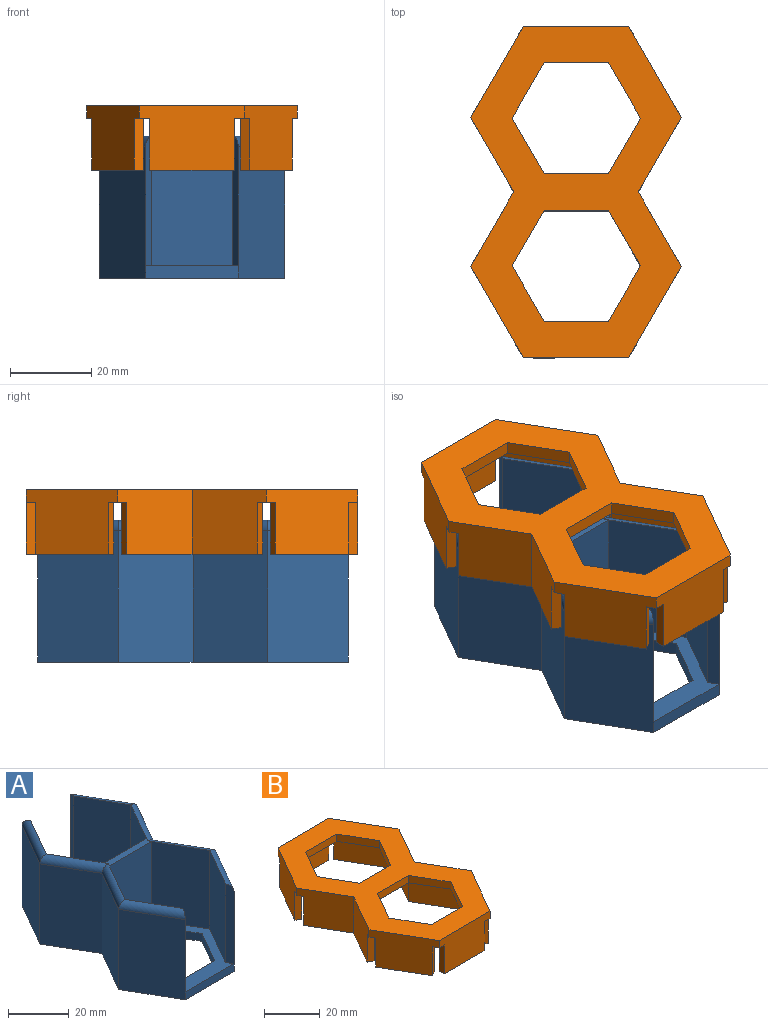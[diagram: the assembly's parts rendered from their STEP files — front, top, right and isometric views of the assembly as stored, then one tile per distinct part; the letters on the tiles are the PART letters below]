
ASSEMBLY  parts=2 mates=2
PART A: 48 faces, bbox 45.5x76.2x34.9 mm
  f0: plane 19.8x2.54mm, normal (0,0,1), area 48.4mm2, adj f4,f6,f41,f42,f45,f46
  f1: plane 31.75x17.15mm, normal (0.87,-0.5,0), area 628.6mm2, adj f20,f28,f37,f40
  f2: plane 31.75x17.15mm, normal (-0.87,-0.5,0), area 628.6mm2, adj f3,f28,f36,f47
  f3: plane 31.75x17.15mm, normal (-0.87,0.5,0), area 628.6mm2, adj f2,f4,f28,f46
  f4: plane 31.75x19.8mm, normal (0,1,0), area 628.6mm2, adj f0,f3,f20,f28
  f5: plane 31.75x17.15mm, normal (0.87,-0.5,0), area 628.6mm2, adj f6,f18,f35,f42
  f6: plane 31.75x19.8mm, normal (0,-1,0), area 628.6mm2, adj f0,f5,f7,f35
  f7: plane 31.75x17.15mm, normal (-0.87,-0.5,0), area 628.6mm2, adj f6,f8,f35,f45
  f8: plane 31.75x17.15mm, normal (-0.87,0.5,0), area 628.6mm2, adj f7,f35,f39,f44
  f9: plane 32.39x19.69mm, normal (0.87,-0.5,0), area 736.1mm2, adj f10,f19,f21,f39,f44
  f10: plane 32.39x18.42mm, normal (0.87,0.5,0), area 688.6mm2, adj f9,f11,f21,f45
  f11: plane 32.39x18.42mm, normal (0.87,-0.5,0), area 688.6mm2, adj f10,f12,f21,f46
  f12: plane 32.39x19.69mm, normal (0.87,0.5,0), area 736.1mm2, adj f11,f13,f21,f36,f47
  f13: plane 22.73x3.18mm, normal (0,1,0), area 72.2mm2, adj f12,f14,f21,f28
  f14: plane 32.39x19.69mm, normal (-0.87,0.5,0), area 736.1mm2, adj f13,f15,f21,f37,f40
  f15: plane 32.39x18.42mm, normal (-0.87,-0.5,0), area 688.6mm2, adj f14,f16,f21,f41
  f16: plane 32.39x18.42mm, normal (-0.87,0.5,0), area 688.6mm2, adj f15,f17,f21,f42
  f17: plane 32.39x19.69mm, normal (-0.87,-0.5,0), area 736.1mm2, adj f16,f19,f21,f38,f43
  f18: plane 31.75x17.15mm, normal (0.87,0.5,0), area 628.6mm2, adj f5,f35,f38,f43
  f19: plane 22.73x3.18mm, normal (0,-1,0), area 72.2mm2, adj f9,f17,f21,f35
  f20: plane 31.75x17.15mm, normal (0.87,0.5,0), area 628.6mm2, adj f1,f4,f28,f41
  f21: plane 76.2x45.46mm, normal (0,0,-1), area 1273mm2, adj f9,f10,f11,f12,f13,f14,f15,f16
  f22: plane 13.97x8.07mm, normal (-0.87,0.5,0), area 51.2mm2, adj f21,f23,f27,f28
  f23: plane 16.13x3.18mm, normal (0,1,0), area 51.2mm2, adj f21,f22,f24,f28
  f24: plane 13.97x8.07mm, normal (0.87,0.5,0), area 51.2mm2, adj f21,f23,f25,f28
  f25: plane 13.97x8.07mm, normal (0.87,-0.5,0), area 51.2mm2, adj f21,f24,f26,f28
  f26: plane 16.13x3.18mm, normal (0,-1,0), area 51.2mm2, adj f21,f25,f27,f28
  f27: plane 13.97x8.07mm, normal (-0.87,-0.5,0), area 51.2mm2, adj f21,f22,f26,f28
  f28: plane 39.59x36.83mm, normal (0,0,1), area 396.2mm2, adj f1,f2,f3,f4,f13,f20,f22,f23
  f29: plane 13.97x8.07mm, normal (-0.87,0.5,0), area 51.2mm2, adj f21,f30,f34,f35
  f30: plane 16.13x3.18mm, normal (0,1,0), area 51.2mm2, adj f21,f29,f31,f35
  f31: plane 13.97x8.07mm, normal (0.87,0.5,0), area 51.2mm2, adj f21,f30,f32,f35
  f32: plane 13.97x8.07mm, normal (0.87,-0.5,0), area 51.2mm2, adj f21,f31,f33,f35
  f33: plane 16.13x3.18mm, normal (0,-1,0), area 51.2mm2, adj f21,f32,f34,f35
  f34: plane 13.97x8.07mm, normal (-0.87,-0.5,0), area 51.2mm2, adj f21,f29,f33,f35
  f35: plane 39.59x36.83mm, normal (0,0,1), area 396.2mm2, adj f5,f6,f7,f8,f18,f19,f29,f30
  f36: plane 31.75x2.54mm, normal (-0.87,0.5,0), area 91.5mm2, adj f2,f12,f28,f47
  f37: plane 31.75x2.54mm, normal (0.87,0.5,0), area 91.5mm2, adj f1,f14,f28,f40
  f38: plane 31.75x2.54mm, normal (0.87,-0.5,0), area 91.5mm2, adj f17,f18,f35,f43
  f39: plane 31.75x2.54mm, normal (-0.87,-0.5,0), area 91.5mm2, adj f8,f9,f35,f44
  f40: cylinder r=2.54mm len=20.96mm, axis (0.5,0.87,0), area 86.4mm2, adj f1,f14,f37,f41
  f41: cylinder r=2.54mm len=20.96mm, axis (-0.5,0.87,0), area 84.8mm2, adj f0,f15,f20,f40,f42
  f42: cylinder r=2.54mm len=20.96mm, axis (0.5,0.87,0), area 84.8mm2, adj f0,f5,f16,f41,f43
  f43: cylinder r=2.54mm len=20.96mm, axis (-0.5,0.87,0), area 86.4mm2, adj f17,f18,f38,f42
  f44: cylinder r=2.54mm len=20.96mm, axis (-0.5,-0.87,0), area 86.4mm2, adj f8,f9,f39,f45
  f45: cylinder r=2.54mm len=20.96mm, axis (0.5,-0.87,0), area 84.8mm2, adj f0,f7,f10,f44,f46
  f46: cylinder r=2.54mm len=20.96mm, axis (-0.5,-0.87,0), area 84.8mm2, adj f0,f3,f11,f45,f47
  f47: cylinder r=2.54mm len=20.96mm, axis (0.5,-0.87,0), area 86.4mm2, adj f2,f12,f36,f46
PART B: 58 faces, bbox 51.8x81.5x15.9 mm
  f0: plane 19.35x12.64mm, normal (0,0,-1), area 53mm2, adj f18,f21,f42,f44
  f1: plane 19.35x12.64mm, normal (0,0,-1), area 53mm2, adj f13,f16,f46,f49
  f2: plane 34.72x12.22mm, normal (0,0,-1), area 98.1mm2, adj f14,f20,f26,f29,f47,f55
  f3: plane 20.73x2.54mm, normal (0,0,-1), area 52.7mm2, adj f9,f24,f52,f56
  f4: plane 19.35x12.64mm, normal (0,0,-1), area 53mm2, adj f8,f25,f54,f57
  f5: plane 19.35x12.64mm, normal (0,0,-1), area 53mm2, adj f10,f11,f50,f53
  f6: plane 34.72x12.22mm, normal (0,0,-1), area 98.1mm2, adj f15,f19,f27,f28,f43,f51
  f7: plane 20.73x2.54mm, normal (0,0,-1), area 52.7mm2, adj f12,f17,f45,f48
  f8: plane 18.08x12.7mm, normal (0.87,-0.5,0), area 265.1mm2, adj f4,f22,f54,f57
  f9: plane 20.73x12.7mm, normal (0,-1,0), area 263.3mm2, adj f3,f22,f52,f56
  f10: plane 18.08x12.7mm, normal (-0.87,-0.5,0), area 265.1mm2, adj f5,f22,f50,f53
  f11: plane 22.48x15.88mm, normal (0.87,0.5,0), area 347.5mm2, adj f5,f22,f23,f24,f27,f50,f53
  f12: plane 25.81x15.88mm, normal (0,-1,0), area 345.2mm2, adj f7,f13,f21,f22,f23,f45,f48
  f13: plane 22.48x15.88mm, normal (-0.87,-0.5,0), area 347.5mm2, adj f1,f12,f14,f22,f23,f46,f49
  f14: plane 18.29x15.88mm, normal (-0.87,0.5,0), area 303mm2, adj f2,f13,f22,f23,f26,f47
  f15: plane 18.29x15.88mm, normal (0.87,0.5,0), area 303mm2, adj f6,f21,f22,f23,f27,f43
  f16: plane 18.08x12.7mm, normal (0.87,0.5,0), area 265.1mm2, adj f1,f22,f46,f49
  f17: plane 20.73x12.7mm, normal (0,1,0), area 263.3mm2, adj f7,f22,f45,f48
  f18: plane 18.08x12.7mm, normal (-0.87,0.5,0), area 265.1mm2, adj f0,f22,f42,f44
  f19: plane 17.36x12.7mm, normal (-0.87,-0.5,0), area 254.6mm2, adj f6,f22,f28,f43
  f20: plane 17.36x12.7mm, normal (0.87,-0.5,0), area 254.6mm2, adj f2,f22,f29,f47
  f21: plane 22.48x15.88mm, normal (0.87,-0.5,0), area 347.5mm2, adj f0,f12,f15,f22,f23,f42,f44
  f22: plane 81.53x51.77mm, normal (0,0,-1), area 1444.3mm2, adj f8,f9,f10,f11,f12,f13,f14,f15
  f23: plane 81.53x51.77mm, normal (0,0,1), area 1957.9mm2, adj f11,f12,f13,f14,f15,f21,f24,f25
  f24: plane 25.81x15.88mm, normal (0,1,0), area 345.2mm2, adj f3,f11,f22,f23,f25,f52,f56
  f25: plane 22.48x15.88mm, normal (-0.87,0.5,0), area 347.5mm2, adj f4,f22,f23,f24,f26,f54,f57
  f26: plane 18.29x15.88mm, normal (-0.87,-0.5,0), area 303mm2, adj f2,f14,f22,f23,f25,f55
  f27: plane 18.29x15.88mm, normal (0.87,-0.5,0), area 303mm2, adj f6,f11,f15,f22,f23,f51
  f28: plane 17.36x12.7mm, normal (-0.87,0.5,0), area 254.6mm2, adj f6,f19,f22,f51
  f29: plane 17.36x12.7mm, normal (0.87,0.5,0), area 254.6mm2, adj f2,f20,f22,f55
  f30: plane 13.66x7.89mm, normal (-0.87,-0.5,0), area 50.1mm2, adj f22,f23,f31,f35
  f31: plane 15.78x3.18mm, normal (0,-1,0), area 50.1mm2, adj f22,f23,f30,f32
  f32: plane 13.66x7.89mm, normal (0.87,-0.5,0), area 50.1mm2, adj f22,f23,f31,f33
  f33: plane 13.66x7.89mm, normal (0.87,0.5,0), area 50.1mm2, adj f22,f23,f32,f34
  f34: plane 15.78x3.18mm, normal (0,1,0), area 50.1mm2, adj f22,f23,f33,f35
  f35: plane 13.66x7.89mm, normal (-0.87,0.5,0), area 50.1mm2, adj f22,f23,f30,f34
  f36: plane 13.66x7.89mm, normal (-0.87,0.5,0), area 50.1mm2, adj f22,f23,f37,f41
  f37: plane 15.78x3.18mm, normal (0,1,0), area 50.1mm2, adj f22,f23,f36,f38
  f38: plane 13.66x7.89mm, normal (0.87,0.5,0), area 50.1mm2, adj f22,f23,f37,f39
  f39: plane 13.66x7.89mm, normal (0.87,-0.5,0), area 50.1mm2, adj f22,f23,f38,f40
  f40: plane 15.78x3.18mm, normal (0,-1,0), area 50.1mm2, adj f22,f23,f39,f41
  f41: plane 13.66x7.89mm, normal (-0.87,-0.5,0), area 50.1mm2, adj f22,f23,f36,f40
  f42: plane 12.7x2.2mm, normal (0.5,0.87,0), area 32.3mm2, adj f0,f18,f21,f22
  f43: plane 12.7x2.2mm, normal (0.5,-0.87,0), area 32.3mm2, adj f6,f15,f19,f22
  f44: plane 12.7x2.2mm, normal (-0.5,-0.87,0), area 32.3mm2, adj f0,f18,f21,f22
  f45: plane 12.7x2.54mm, normal (1,0,0), area 32.3mm2, adj f7,f12,f17,f22
  f46: plane 12.7x2.2mm, normal (-0.5,0.87,0), area 32.3mm2, adj f1,f13,f16,f22
  f47: plane 12.7x2.2mm, normal (-0.5,-0.87,0), area 32.3mm2, adj f2,f14,f20,f22
  f48: plane 12.7x2.54mm, normal (-1,0,0), area 32.3mm2, adj f7,f12,f17,f22
  f49: plane 12.7x2.2mm, normal (0.5,-0.87,0), area 32.3mm2, adj f1,f13,f16,f22
  f50: plane 12.7x2.2mm, normal (0.5,-0.87,0), area 32.3mm2, adj f5,f10,f11,f22
  f51: plane 12.7x2.2mm, normal (0.5,0.87,0), area 32.3mm2, adj f6,f22,f27,f28
  f52: plane 12.7x2.54mm, normal (1,0,0), area 32.3mm2, adj f3,f9,f22,f24
  f53: plane 12.7x2.2mm, normal (-0.5,0.87,0), area 32.3mm2, adj f5,f10,f11,f22
  f54: plane 12.7x2.2mm, normal (-0.5,-0.87,0), area 32.3mm2, adj f4,f8,f22,f25
  f55: plane 12.7x2.2mm, normal (-0.5,0.87,0), area 32.3mm2, adj f2,f22,f26,f29
  f56: plane 12.7x2.54mm, normal (-1,0,0), area 32.3mm2, adj f3,f9,f22,f24
  f57: plane 12.7x2.2mm, normal (0.5,0.87,0), area 32.3mm2, adj f4,f8,f22,f25
PLACE A t=(-4.96,26.82,-17.63)mm
PLACE B t=(-4.88,8.66,8.98)mm
MATE planar B.f16 <-> A.f17  axis (0.87,0.5,0) through (-16.93,-28.64,8.98)mm
MATE planar B.f18 <-> A.f9  axis (-0.87,0.5,0) through (12.24,-19.6,15.33)mm
